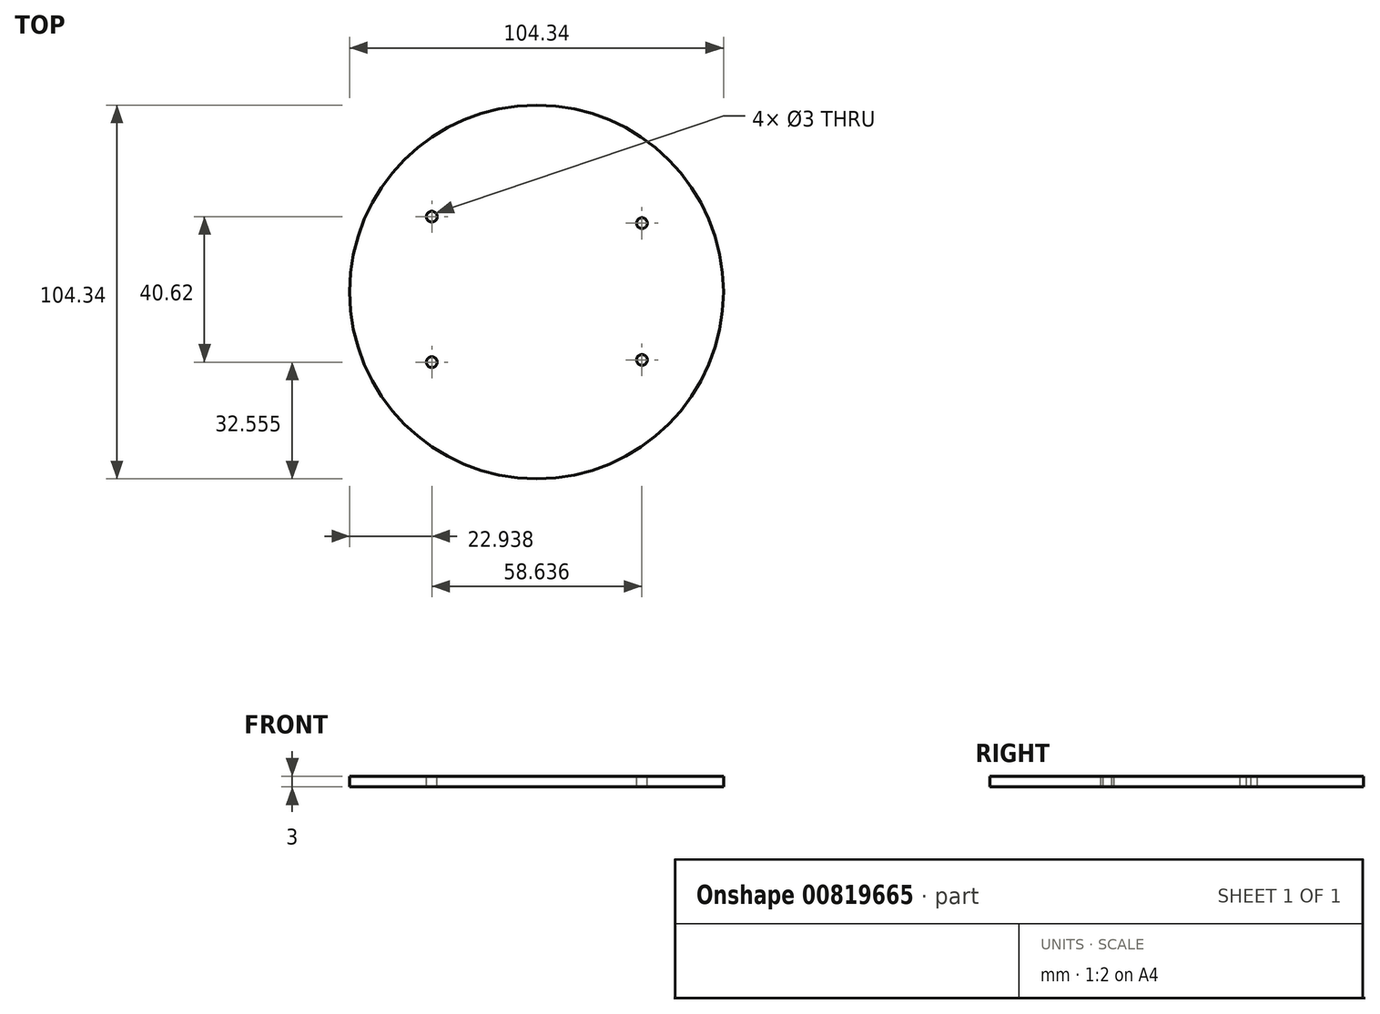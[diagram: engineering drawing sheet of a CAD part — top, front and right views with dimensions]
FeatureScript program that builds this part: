
annotation { "Feature Type Name" : "Feature", "Feature Type Description" : "" }
export const myFeature = defineFeature(function(context is Context, id is Id, definition is map)
    precondition{}
    {
        {
            var Q0;
            Q0=qCreatedBy(makeId("Top.planeOp"),FACE);
            var sketch = newSketch(context, id + "F0", { "sketchPlane" : qUnion([Q0])});
            skCircle(sketch, "E0", {"center": v(0, 0) * mm, "radius": 52.17 * mm});
            skSolve(sketch);
        }
        {
            var Q0;
            Q0=makeQuery(id+"F0.imprint","IMPRINT",FACE,{"disambiguationData":[TD([[makeQuery(id+"F0.imprint","IMPRINT",EDGE,{"derivedFrom":sQuery(id+"F0.wireOp",EDGE,"E0")}),1.0]])]});
            var Q1;
            Q1 = qSketchRegion(id + "F0", true);
            extrude(context, id + "F1", {"entities" : qUnion([Q0, Q1]), "depth" : 3 * mm, "offsetDistance" : 25.4 * mm});
        }
        {
            var Q0;
            Q0=makeQuery(id+"F1.opExtrude","CAP_FACE",FACE,{"disambiguationData":[OSD([sQuery(id+"F0.wireOp",EDGE,"E0")])],"isStart":true});
            var sketch = newSketch(context, id + "F2", { "sketchPlane" : qUnion([Q0])});
            skLineSegment(sketch, "E1", {"start": v(-14.46, -16.74) * mm, "end": v(9.54, -16.74) * mm});
            skSolve(sketch);
        }
        {
            var Q0;
            Q0=sQuery(id+"F2.wireOp",VERTEX,"E1.start");
            var Q1;
            Q1=sQuery(id+"F2.wireOp",VERTEX,"E1.end");
            var Q2;
            Q2=makeQuery(id+"F1.opExtrude","SWEPT_BODY",BODY,{"disambiguationData":[OSD([sQuery(id+"F0.wireOp",EDGE,"E0")])]});
            hole(context, id + "F3", {"style" : HoleStyle.SIMPLE, "endStyle" : HoleEndStyle.THROUGH, "holeDiameter" : 3 * mm, "majorDiameter" : 5 * mm, "isTappedThrough" : true, "tappedDepth" : 12 * mm, "tapClearance" : 3, "locations" : qUnion([Q0, Q1]), "scope" : qUnion([Q2])});
        }
        {
            var Q0;
            Q0=makeQuery(id+"F1.opExtrude","SWEPT_BODY",BODY,{"disambiguationData":[OSD([sQuery(id+"F0.wireOp",EDGE,"E0")])]});
            var Q1;
            Q1=qCreatedBy(makeId("Front.planeOp"),FACE);
            mirror(context, id + "F4", {"operationType" : NewBodyOperationType.ADD, "entities" : qUnion([Q0]), "mirrorPlane" : qUnion([Q1])});
        }
        {
            var Q0;
            {var subQ0=makeQuery(id+"F1.opExtrude","CAP_FACE",FACE,{"disambiguationData":[OSD([sQuery(id+"F0.wireOp",EDGE,"E0")])],"isStart":false});Q0=makeQuery(id+"F4.boolean.opBoolean","MERGE",FACE,{"derivedFrom":[subQ0,makeQuery(id+"F4.opPattern","COPY",FACE,{"derivedFrom":subQ0,"instanceName":"1"})]});}
            var sketch = newSketch(context, id + "F5", { "sketchPlane" : qUnion([Q0])});
            skLineSegment(sketch, "E2", {"start": v(29.4, 19.2) * mm, "end": v(29.4, -18.99) * mm});
            skSolve(sketch);
        }
        {
            var Q0;
            Q0=makeQuery(id+"F5.imprint","IMPRINT",FACE,{"disambiguationData":[TD([[makeQuery(id+"F5.imprint","IMPRINT",EDGE,{"derivedFrom":makeQuery(id+"F1.opExtrude","CAP_EDGE",EDGE,{"disambiguationData":[OSD([sQuery(id+"F0.wireOp",EDGE,"E0")])],"isStart":false})}),1.0]])]});
            var sketch = newSketch(context, id + "F6", { "sketchPlane" : qUnion([Q0])});
            skLineSegment(sketch, "E3", {"start": v(-29.23, -19.62) * mm, "end": v(-29.23, 21) * mm});
            skSolve(sketch);
        }
        {
            var Q0;
            Q0=sQuery(id+"F6.wireOp",VERTEX,"E3.end");
            var Q1;
            Q1=sQuery(id+"F6.wireOp",VERTEX,"E3.start");
            var Q2;
            Q2=sQuery(id+"F5.wireOp",VERTEX,"E2.start");
            var Q3;
            Q3=sQuery(id+"F5.wireOp",VERTEX,"E2.end");
            var Q4;
            Q4=makeQuery(id+"F1.opExtrude","SWEPT_BODY",BODY,{"disambiguationData":[OSD([sQuery(id+"F0.wireOp",EDGE,"E0")])]});
            hole(context, id + "F7", {"style" : HoleStyle.SIMPLE, "endStyle" : HoleEndStyle.THROUGH, "holeDiameter" : 3 * mm, "majorDiameter" : 5 * mm, "isTappedThrough" : true, "tappedDepth" : 12 * mm, "tapClearance" : 3, "locations" : qUnion([Q0, Q1, Q2, Q3]), "scope" : qUnion([Q4])});
        }
    });
